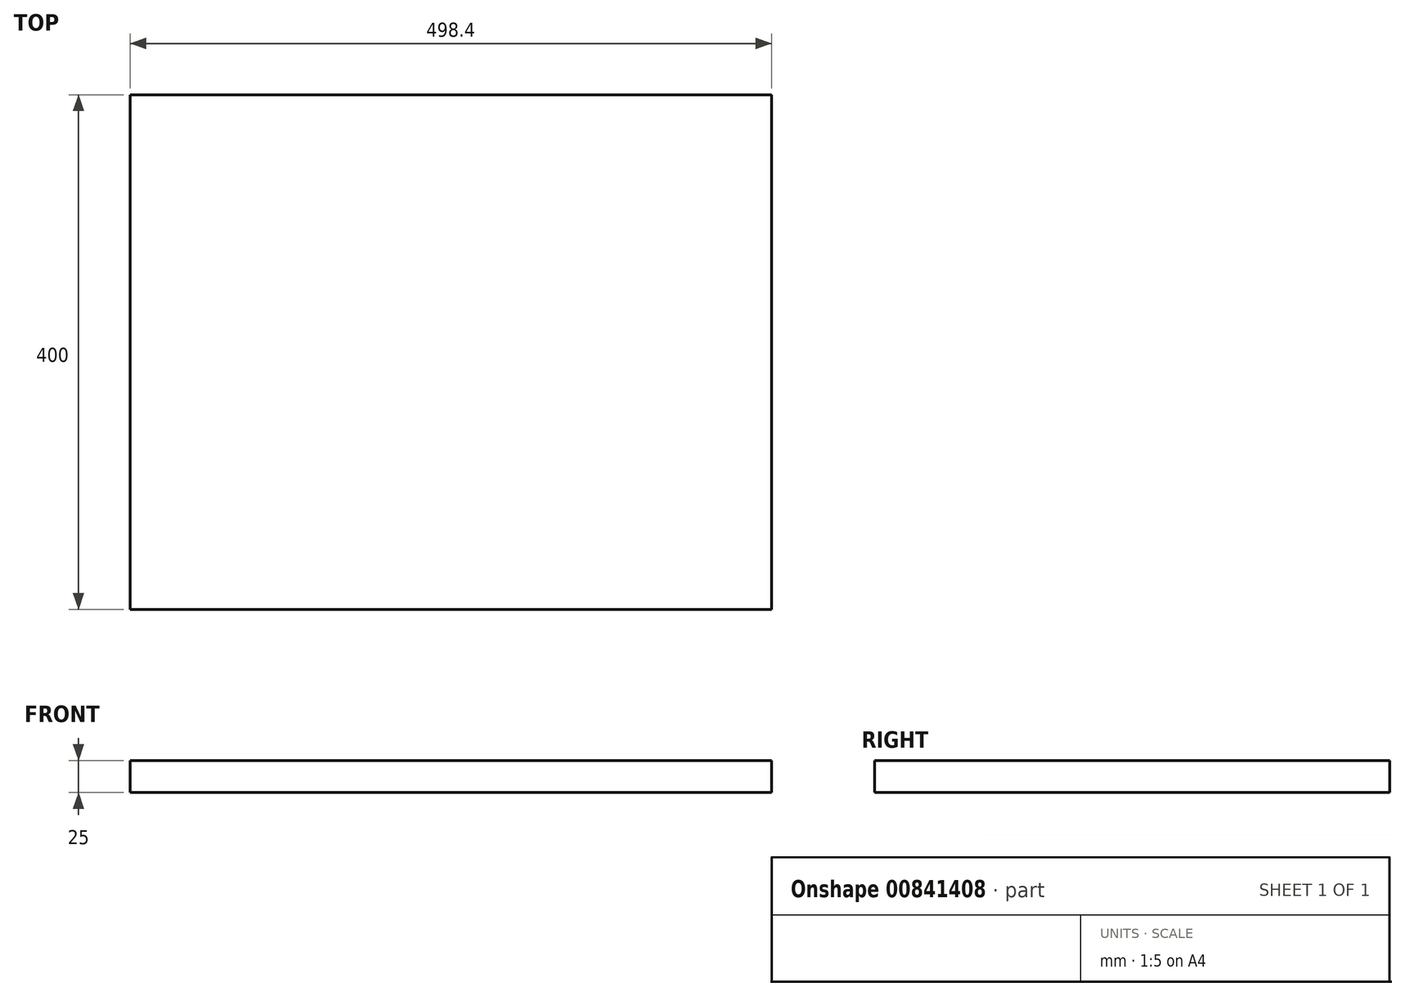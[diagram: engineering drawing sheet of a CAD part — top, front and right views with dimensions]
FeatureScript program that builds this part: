
annotation { "Feature Type Name" : "Feature", "Feature Type Description" : "" }
export const myFeature = defineFeature(function(context is Context, id is Id, definition is map)
    precondition{}
    {
        {
            var Q0;
            Q0=qCreatedBy(makeId("Top.planeOp"),FACE);
            var sketch = newSketch(context, id + "F0", { "sketchPlane" : qUnion([Q0])});
            skLineSegment(sketch, "E0.bottom", {"start": v(249.2, 200) * mm, "end": v(-249.2, 200) * mm});
            skLineSegment(sketch, "E0.top", {"start": v(249.2, -200) * mm, "end": v(-249.2, -200) * mm});
            skLineSegment(sketch, "E0.left", {"start": v(249.2, 200) * mm, "end": v(249.2, -200) * mm});
            skLineSegment(sketch, "E0.right", {"start": v(-249.2, 200) * mm, "end": v(-249.2, -200) * mm});
            skPoint(sketch, "E0.middle", {"position": v(0, 0) * mm});
            skSolve(sketch);
        }
        {
            var Q0;
            Q0 = qSketchRegion(id + "F0", true);
            extrude(context, id + "F1", {"entities" : qUnion([Q0]), "depth" : 25 * mm, "offsetDistance" : 25 * mm});
        }
    });
